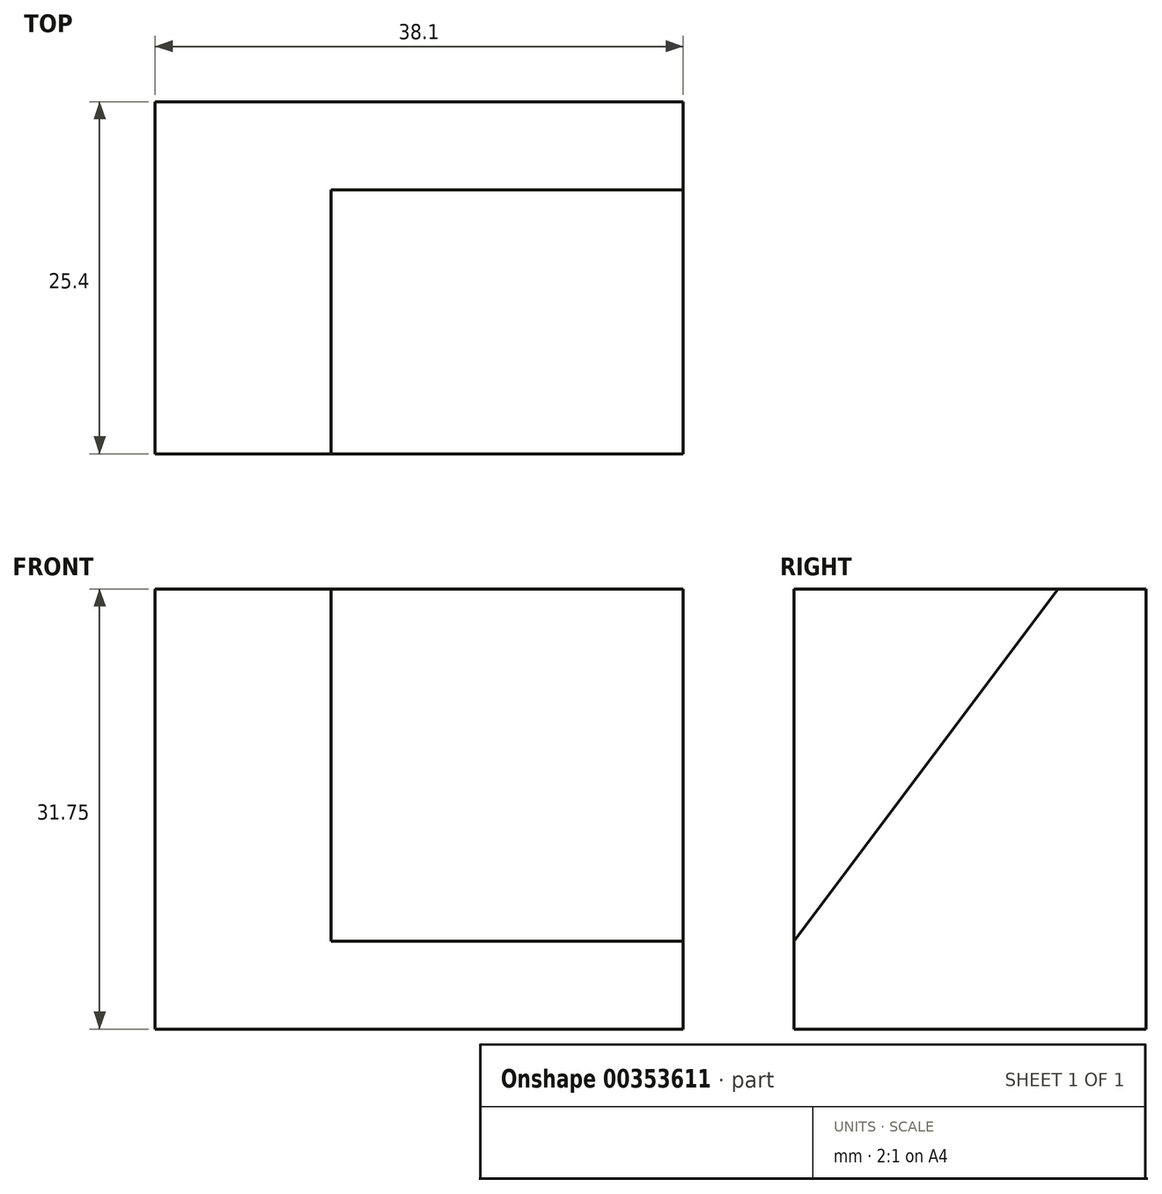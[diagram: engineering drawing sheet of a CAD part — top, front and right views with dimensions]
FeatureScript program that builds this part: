
annotation { "Feature Type Name" : "Feature", "Feature Type Description" : "" }
export const myFeature = defineFeature(function(context is Context, id is Id, definition is map)
    precondition{}
    {
        {
            var Q0;
            Q0=qCreatedBy(makeId("Right.planeOp"),FACE);
            var sketch = newSketch(context, id + "F0", { "sketchPlane" : qUnion([Q0])});
            skLineSegment(sketch, "E0", {"start": v(0, 0) * mm, "end": v(0, 6.35) * mm});
            skLineSegment(sketch, "E1", {"start": v(0, 6.35) * mm, "end": v(19.05, 31.75) * mm});
            skLineSegment(sketch, "E2", {"start": v(19.05, 31.75) * mm, "end": v(25.4, 31.75) * mm});
            skLineSegment(sketch, "E3", {"start": v(25.4, 31.75) * mm, "end": v(25.4, 0) * mm});
            skLineSegment(sketch, "E4", {"start": v(0, 0) * mm, "end": v(25.4, 0) * mm});
            skSolve(sketch);
        }
        {
            var Q0;
            Q0=makeQuery(id+"F0.imprint","IMPRINT",FACE,{"disambiguationData":[TD([[makeQuery(id+"F0.imprint","IMPRINT",EDGE,{"derivedFrom":sQuery(id+"F0.wireOp",EDGE,"E0")}),-1.0]])]});
            extrude(context, id + "F1", {"entities" : qUnion([Q0]), "depth" : 38.1 * mm});
        }
        {
            var Q0;
            Q0=makeQuery(id+"F1.opExtrude","CAP_FACE",FACE,{"disambiguationData":[OSD([sQuery(id+"F0.wireOp",EDGE,"E0"),sQuery(id+"F0.wireOp",EDGE,"E1"),sQuery(id+"F0.wireOp",EDGE,"E2"),sQuery(id+"F0.wireOp",EDGE,"E3"),sQuery(id+"F0.wireOp",EDGE,"E4")])],"isStart":true});
            var sketch = newSketch(context, id + "F2", { "sketchPlane" : qUnion([Q0])});
            skLineSegment(sketch, "E5", {"start": v(-19.05, 31.75) * mm, "end": v(0, 31.75) * mm});
            skLineSegment(sketch, "E6", {"start": v(0, 31.75) * mm, "end": v(0, 6.35) * mm});
            skLineSegment(sketch, "E7", {"start": v(0, 6.35) * mm, "end": v(-19.05, 31.75) * mm});
            skSolve(sketch);
        }
        {
            var Q0;
            Q0=makeQuery(id+"F2.imprint","IMPRINT",FACE,{"disambiguationData":[TD([[makeQuery(id+"F2.imprint","IMPRINT",EDGE,{"derivedFrom":sQuery(id+"F2.wireOp",EDGE,"E5")}),-1.0]])]});
            extrude(context, id + "F3", {"entities" : qUnion([Q0]), "operationType" : NewBodyOperationType.ADD, "oppositeDirection" : true, "depth" : 12.7 * mm});
        }
    });
